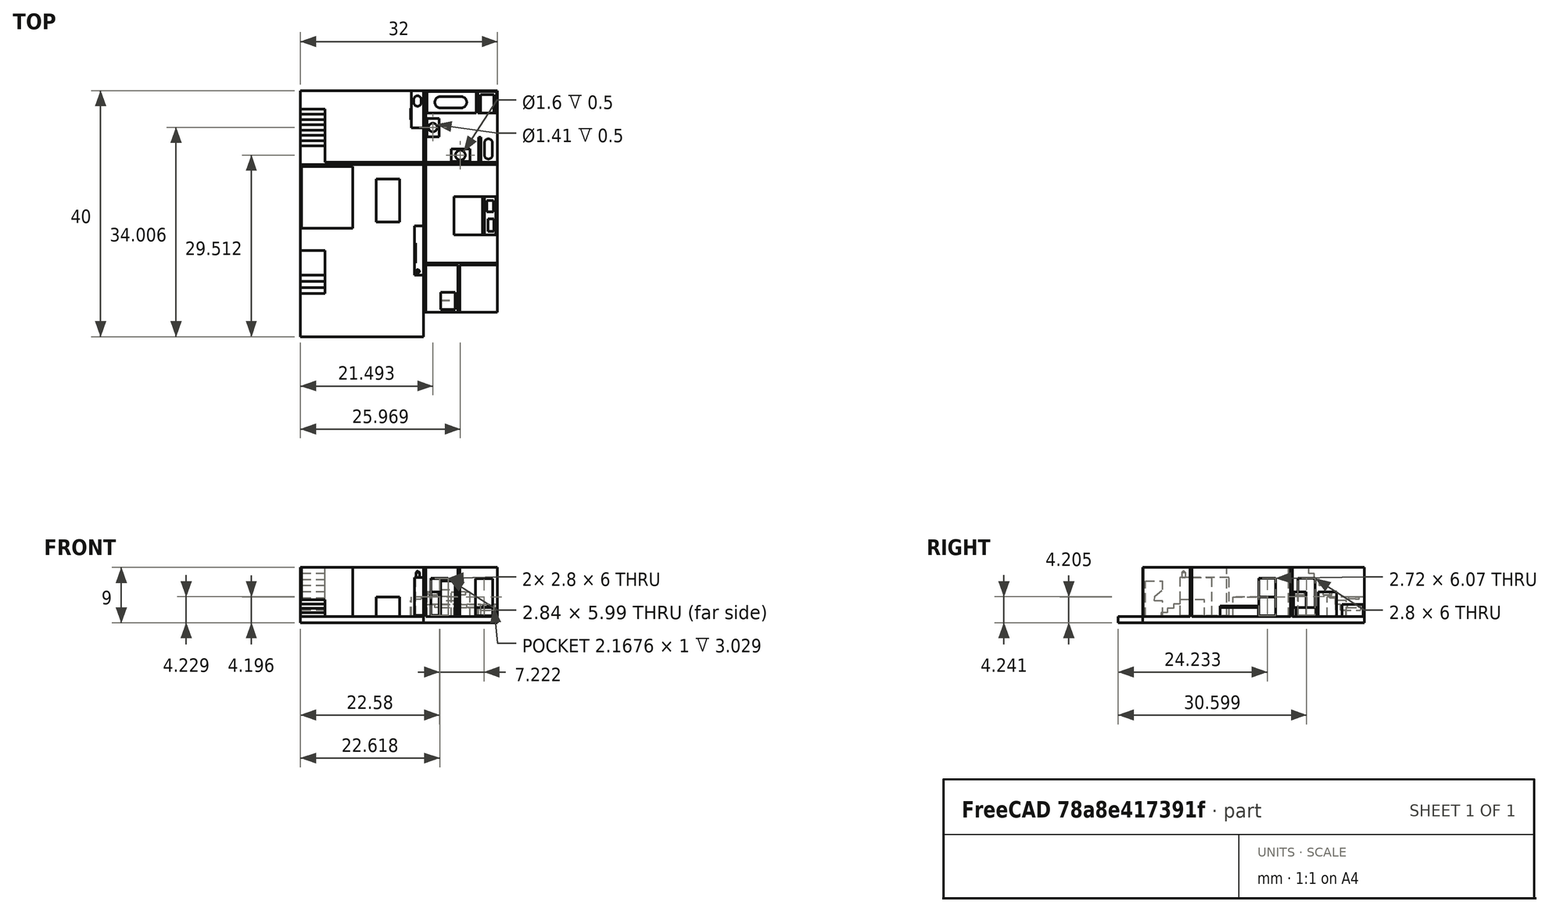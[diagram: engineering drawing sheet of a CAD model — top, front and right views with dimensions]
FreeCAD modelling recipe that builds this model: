
FCSTD DOCUMENT  (FreeCAD 0.19R)
Label: Addition1c
License: All rights reserved
LicenseURL: http://en.wikipedia.org/wiki/All_rights_reserved
objects: Sketcher::SketchObject×28, PartDesign::Pad×17, PartDesign::Pocket×10, PartDesign::Chamfer×1, PartDesign::Body×1, Mesh::Feature×1
note: 85 computed .brp shape members not serialized (recipe doc carries the construction recipe); baked Part::Feature solids carry a one-line shape summary decoded from their .brp

FEATURE [Sketcher::SketchObject] Sketch
  FullyConstrained = true
  MapMode = 5
  Support = -> [XY_Plane]
  sketch-geometry (8):
    g0: LineSegment StartX=0 StartY=-28 StartZ=0 EndX=-20 EndY=-28 EndZ=0
    g1: LineSegment StartX=-20 StartY=-28 StartZ=0 EndX=-20 EndY=0 EndZ=0
    g2: LineSegment StartX=-20 StartY=0 StartZ=0 EndX=-16 EndY=0 EndZ=0
    g3: LineSegment StartX=-16 StartY=0 StartZ=0 EndX=-16 EndY=12 EndZ=0
    g4: LineSegment StartX=-16 StartY=12 StartZ=0 EndX=12 EndY=12 EndZ=0
    g5: LineSegment StartX=12 StartY=12 StartZ=0 EndX=12 EndY=-24 EndZ=0
    g6: LineSegment StartX=12 StartY=-24 StartZ=0 EndX=0 EndY=-24 EndZ=0
    g7: LineSegment StartX=0 StartY=-24 StartZ=0 EndX=0 EndY=-28 EndZ=0
  constraints (24):
    c: Coincident(g0,g1)
    c: Horizontal(g0)
    c: Vertical(g1)
    c: DistanceX(g1) = -20
    c: DistanceY(g0) = -28
    c: Coincident(g1,g2)
    c: PointOnObject(g2,g-1)
    c: Horizontal(g2)
    c: Coincident(g2,g3)
    c: Vertical(g3)
    c: Coincident(g3,g4)
    c: Horizontal(g4)
    c: Coincident(g4,g5)
    c: Vertical(g5)
    c: Coincident(g5,g6)
    c: PointOnObject(g6,g-2)
    c: Coincident(g6,g7)
    c: Coincident(g7,g0)
    c: Vertical(g7)
    c: Horizontal(g6)
    c: Distance(g6) = 12
    c: Distance(g3) = 12
    c: DistanceY(g6) = -24
    c: DistanceX(g2) = -16
FEATURE [PartDesign::Pad] Pad  label="foundation"
  Direction = (1,1,1)
  Length = 1
  Length2 = 100
  Profile = -> Sketch
  Type = 0
FEATURE [Sketcher::SketchObject] Sketch004
  FullyConstrained = true
  MapMode = 5
  Placement = pos=(-16,0,0) rot=(0.57735,-0.57735,-0.57735;2.0944rad)
  Support = -> [Pad]
  sketch-geometry (20):
    g0: LineSegment StartX=-12 StartY=0 StartZ=0 EndX=-12 EndY=1 EndZ=0
    g1: LineSegment StartX=-12 StartY=1 StartZ=0 EndX=-9 EndY=1 EndZ=0
    g2: LineSegment StartX=-9 StartY=1 StartZ=0 EndX=-9 EndY=2 EndZ=0
    g3: LineSegment StartX=-9 StartY=2 StartZ=0 EndX=-8.14286 EndY=2 EndZ=0
    g4: LineSegment StartX=-8.14286 StartY=2 StartZ=0 EndX=-8.14286 EndY=3 EndZ=0
    g5: LineSegment StartX=-8.14286 StartY=3 StartZ=0 EndX=-7.28571 EndY=3 EndZ=0
    g6: LineSegment StartX=-7.28571 StartY=3 StartZ=0 EndX=-7.28571 EndY=4 EndZ=0
    g7: LineSegment StartX=-7.28571 StartY=4 StartZ=0 EndX=-6.42857 EndY=4 EndZ=0
    g8: LineSegment StartX=-6.42857 StartY=4 StartZ=0 EndX=-6.42857 EndY=5 EndZ=0
    g9: LineSegment StartX=-6.42857 StartY=5 StartZ=0 EndX=-5.57143 EndY=5 EndZ=0
    g10: LineSegment StartX=-5.57143 StartY=5 StartZ=0 EndX=-5.57143 EndY=6 EndZ=0
    g11: LineSegment StartX=-5.57143 StartY=6 StartZ=0 EndX=-4.71429 EndY=6 EndZ=0
    g12: LineSegment StartX=-4.71429 StartY=6 StartZ=0 EndX=-4.71429 EndY=7 EndZ=0
    g13: LineSegment StartX=-4.71429 StartY=7 StartZ=0 EndX=-3.85714 EndY=7 EndZ=0
    g14: LineSegment StartX=-3.85714 StartY=7 StartZ=0 EndX=-3.85714 EndY=8 EndZ=0
    g15: LineSegment StartX=-3.85714 StartY=8 StartZ=0 EndX=-3 EndY=8 EndZ=0
    g16: LineSegment StartX=-3 StartY=8 StartZ=0 EndX=-3 EndY=9 EndZ=0
    g17: LineSegment StartX=-3 StartY=9 StartZ=0 EndX=0 EndY=9 EndZ=0
    g18: LineSegment StartX=0 StartY=9 StartZ=0 EndX=0 EndY=0 EndZ=0
    g19: LineSegment StartX=0 StartY=0 StartZ=0 EndX=-12 EndY=0 EndZ=0
  constraints (59):
    c: PointOnObject(g0,g-1)
    c: Coincident(g0,g1)
    c: Coincident(g1,g2)
    c: Coincident(g2,g3)
    c: Coincident(g3,g4)
    c: Vertical(g4)
    c: Coincident(g4,g5)
    c: Horizontal(g5)
    c: Coincident(g5,g6)
    c: Coincident(g6,g7)
    c: Coincident(g7,g8)
    c: Coincident(g8,g9)
    c: Coincident(g9,g10)
    c: Coincident(g10,g11)
    c: Horizontal(g11)
    c: Coincident(g11,g12)
    c: Coincident(g12,g13)
    c: Coincident(g13,g14)
    c: Coincident(g14,g15)
    c: Coincident(g15,g16)
    c: Coincident(g16,g17)
    c: PointOnObject(g17,g-2)
    c: Coincident(g17,g18)
    c: Coincident(g18,g-1)
    c: Coincident(g18,g19)
    c: Coincident(g19,g0)
    c: DistanceY(g17) = 9
    c: Horizontal(g3)
    c: Horizontal(g7)
    c: Horizontal(g9)
    c: Horizontal(g13)
    c: Horizontal(g15)
    c: Vertical(g6)
    c: Vertical(g8)
    c: Vertical(g12)
    c: Vertical(g10)
    c: Vertical(g14)
    c: Vertical(g16)
    c: Vertical(g2)
    c: Equal(g2,g4)
    c: Equal(g4,g6)
    c: Equal(g6,g8)
    c: Equal(g8,g10)
    c: Equal(g10,g12)
    c: Equal(g12,g14)
    c: Equal(g14,g16)
    c: Distance(g17) = 3
    c: Equal(g3,g5)
    c: Equal(g5,g7)
    c: Equal(g7,g9)
    c: Equal(g9,g11)
    c: Equal(g11,g13)
    c: Equal(g13,g15)
    c: Horizontal(g1)
    c: Horizontal(g17)
    c: Distance(g1) = 3
    c: Vertical(g0)
    c: Distance(g0) = 1
    c: DistanceX(g0) = -12
FEATURE [Sketcher::SketchObject] Sketch007
  FullyConstrained = true
  MapMode = 5
  Placement = pos=(0,0,1) rot=(0,0,1;0rad)
  sketch-geometry (16):
    g0: LineSegment StartX=0.33 StartY=12 StartZ=0 EndX=0.33 EndY=-24 EndZ=0
    g1: LineSegment StartX=0.33 StartY=-24 StartZ=0 EndX=0 EndY=-24 EndZ=0
    g2: LineSegment StartX=0 StartY=-24 StartZ=0 EndX=0 EndY=12 EndZ=0
    g3: LineSegment StartX=0 StartY=12 StartZ=0 EndX=0.33 EndY=12 EndZ=0
    g4: LineSegment StartX=0.33 StartY=0.33 StartZ=0 EndX=12 EndY=0.33 EndZ=0
    g5: LineSegment StartX=12 StartY=0.33 StartZ=0 EndX=12 EndY=0 EndZ=0
    g6: LineSegment StartX=12 StartY=0 StartZ=0 EndX=0.33 EndY=0 EndZ=0
    g7: LineSegment StartX=0.33 StartY=0 StartZ=0 EndX=0.33 EndY=0.33 EndZ=0
    g8: LineSegment StartX=-16 StartY=0.33 StartZ=0 EndX=0 EndY=0.33 EndZ=0
    g9: LineSegment StartX=0 StartY=0.33 StartZ=0 EndX=0 EndY=0 EndZ=0
    g10: LineSegment StartX=0 StartY=0 StartZ=0 EndX=-16 EndY=0 EndZ=0
    g11: LineSegment StartX=-16 StartY=0 StartZ=0 EndX=-16 EndY=0.33 EndZ=0
    g12: LineSegment StartX=0.33 StartY=-16.33 StartZ=0 EndX=12 EndY=-16.33 EndZ=0
    g13: LineSegment StartX=12 StartY=-16.33 StartZ=0 EndX=12 EndY=-16 EndZ=0
    g14: LineSegment StartX=12 StartY=-16 StartZ=0 EndX=0.33 EndY=-16 EndZ=0
    g15: LineSegment StartX=0.33 StartY=-16 StartZ=0 EndX=0.33 EndY=-16.33 EndZ=0
  constraints (47):
    c: Coincident(g0,g1)
    c: Coincident(g1,g2)
    c: Horizontal(g1)
    c: Vertical(g0)
    c: Vertical(g2)
    c: DistanceY(g2) = 12
    c: PointOnObject(g-1,g2)
    c: Coincident(g3,g2)
    c: Coincident(g3,g0)
    c: Horizontal(g3)
    c: Distance(g3) = 0.33
    c: DistanceY(g0) = -24
    c: Coincident(g4,g5)
    c: Coincident(g5,g6)
    c: Coincident(g6,g7)
    c: Coincident(g7,g4)
    c: Horizontal(g4)
    c: Horizontal(g6)
    c: Vertical(g5)
    c: Vertical(g7)
    c: PointOnObject(g5,g-1)
    c: Coincident(g8,g9)
    c: Coincident(g9,g10)
    c: Coincident(g10,g11)
    c: Coincident(g11,g8)
    c: Horizontal(g8)
    c: Horizontal(g10)
    c: Vertical(g9)
    c: Vertical(g11)
    c: Coincident(g9,g-1)
    c: Coincident(g12,g13)
    c: Coincident(g13,g14)
    c: Coincident(g14,g15)
    c: Coincident(g15,g12)
    c: Horizontal(g12)
    c: Horizontal(g14)
    c: Vertical(g13)
    c: Vertical(g15)
    c: PointOnObject(g12,g0)
    c: Distance(g11) = 0.33
    c: Distance(g5) = 0.33
    c: DistanceX(g4) = 12
    c: DistanceX(g8) = -16
    c: PointOnObject(g4,g0)
    c: Distance(g13) = 0.33
    c: Distance(g0,g14) = 8
    c: DistanceX(g13) = 12
FEATURE [PartDesign::Pad] Pad004  label="wall"
  BaseFeature = -> Pad
  Direction = (1,1,1)
  Length = 8
  Length2 = 100
  Profile = -> Sketch007
  Type = 0
FEATURE [PartDesign::Pad] Pad005  label="stairs001"
  BaseFeature = -> Pad004
  Direction = (1,1,1)
  Length = 4
  Length2 = 100
  Profile = -> Sketch004
  Type = 0
FEATURE [Sketcher::SketchObject] Sketch008
  FullyConstrained = false
  MapMode = 5
  Placement = pos=(0,-16.33,0) rot=(1,0,0;1.5708rad)
  Support = -> [Pad005]
  sketch-geometry (8):
    g0: LineSegment StartX=1.18012 StartY=7.22945 StartZ=0 EndX=3.98012 EndY=7.22945 EndZ=0
    g1: LineSegment StartX=3.98012 StartY=7.22945 StartZ=0 EndX=3.98012 EndY=1.22945 EndZ=0
    g2: LineSegment StartX=3.98012 StartY=1.22945 StartZ=0 EndX=1.18012 EndY=1.22945 EndZ=0
    g3: LineSegment StartX=1.18012 StartY=1.22945 StartZ=0 EndX=1.18012 EndY=7.22945 EndZ=0
    g4: LineSegment StartX=8.40186 StartY=7.15703 StartZ=0 EndX=11.2019 EndY=7.15703 EndZ=0
    g5: LineSegment StartX=11.2019 StartY=7.15703 StartZ=0 EndX=11.2019 EndY=1.15703 EndZ=0
    g6: LineSegment StartX=11.2019 StartY=1.15703 StartZ=0 EndX=8.40186 EndY=1.15703 EndZ=0
    g7: LineSegment StartX=8.40186 StartY=1.15703 StartZ=0 EndX=8.40186 EndY=7.15703 EndZ=0
  constraints (20):
    c: Coincident(g0,g1)
    c: Coincident(g1,g2)
    c: Coincident(g2,g3)
    c: Coincident(g3,g0)
    c: Horizontal(g0)
    c: Horizontal(g2)
    c: Vertical(g1)
    c: Vertical(g3)
    c: Coincident(g4,g5)
    c: Coincident(g5,g6)
    c: Coincident(g6,g7)
    c: Coincident(g7,g4)
    c: Horizontal(g4)
    c: Horizontal(g6)
    c: Vertical(g5)
    c: Vertical(g7)
    c: Distance(g4) = 2.8
    c: Distance(g0) = 2.8
    c: Distance(g1) = 6
    c: Distance(g7) = 6
FEATURE [PartDesign::Pocket] Pocket
  BaseFeature = -> Pad005
  Length = 5
  Length2 = 100
  Profile = -> Sketch008
  Type = 0
FEATURE [Sketcher::SketchObject] Sketch009
  FullyConstrained = false
  MapMode = 5
  Placement = pos=(0,0,0) rot=(1,0,0;1.5708rad)
  Support = -> [Pocket]
  sketch-geometry (4):
    g0: LineSegment StartX=1.19795 StartY=7.19291 StartZ=0 EndX=4.03725 EndY=7.19291 EndZ=0
    g1: LineSegment StartX=4.03725 StartY=7.19291 StartZ=0 EndX=4.03725 EndY=1.19882 EndZ=0
    g2: LineSegment StartX=4.03725 StartY=1.19882 StartZ=0 EndX=1.19795 EndY=1.19882 EndZ=0
    g3: LineSegment StartX=1.19795 StartY=1.19882 StartZ=0 EndX=1.19795 EndY=7.19291 EndZ=0
  constraints (8):
    c: Coincident(g0,g1)
    c: Coincident(g1,g2)
    c: Coincident(g2,g3)
    c: Coincident(g3,g0)
    c: Horizontal(g0)
    c: Horizontal(g2)
    c: Vertical(g1)
    c: Vertical(g3)
FEATURE [PartDesign::Pocket] Pocket001
  BaseFeature = -> Pocket
  Length = 5
  Length2 = 100
  Profile = -> Sketch009
  Type = 0
FEATURE [Sketcher::SketchObject] Sketch010
  FullyConstrained = false
  MapMode = 5
  Placement = pos=(0.33,0,0) rot=(0.57735,0.57735,0.57735;2.0944rad)
  Support = -> [Pocket001]
  sketch-geometry (4):
    g0: LineSegment StartX=1.19868 StartY=7.24093 StartZ=0 EndX=3.99868 EndY=7.24093 EndZ=0
    g1: LineSegment StartX=3.99868 StartY=7.24093 StartZ=0 EndX=3.99868 EndY=1.24093 EndZ=0
    g2: LineSegment StartX=3.99868 StartY=1.24093 StartZ=0 EndX=1.19868 EndY=1.24093 EndZ=0
    g3: LineSegment StartX=1.19868 StartY=1.24093 StartZ=0 EndX=1.19868 EndY=7.24093 EndZ=0
  constraints (10):
    c: Coincident(g0,g1)
    c: Coincident(g1,g2)
    c: Coincident(g2,g3)
    c: Coincident(g3,g0)
    c: Horizontal(g0)
    c: Horizontal(g2)
    c: Vertical(g1)
    c: Vertical(g3)
    c: Distance(g0) = 2.8
    c: Distance(g1) = 6
FEATURE [PartDesign::Pocket] Pocket002
  BaseFeature = -> Pocket001
  Length = 5
  Length2 = 100
  Profile = -> Sketch010
  Type = 0
FEATURE [Sketcher::SketchObject] Sketch011
  FullyConstrained = false
  MapMode = 5
  Placement = pos=(0,0,1) rot=(0,0,1;0rad)
  Support = -> [Pocket002]
  sketch-geometry (8):
    g0: LineSegment StartX=0.512815 StartY=11.8677 StartZ=0 EndX=8.51282 EndY=11.8677 EndZ=0
    g1: LineSegment StartX=8.51282 StartY=11.8677 StartZ=0 EndX=8.51282 EndY=8.36765 EndZ=0
    g2: LineSegment StartX=8.51282 StartY=8.36765 StartZ=0 EndX=0.512815 EndY=8.36765 EndZ=0
    g3: LineSegment StartX=0.512815 StartY=8.36765 StartZ=0 EndX=0.512815 EndY=11.8677 EndZ=0
    g4: LineSegment StartX=8.80064 StartY=11.8358 StartZ=0 EndX=11.8627 EndY=11.8358 EndZ=0
    g5: LineSegment StartX=11.8627 StartY=11.8358 StartZ=0 EndX=11.8627 EndY=8.34693 EndZ=0
    g6: LineSegment StartX=11.8627 StartY=8.34693 StartZ=0 EndX=8.80064 EndY=8.34693 EndZ=0
    g7: LineSegment StartX=8.80064 StartY=8.34693 StartZ=0 EndX=8.80064 EndY=11.8358 EndZ=0
  constraints (18):
    c: Coincident(g0,g1)
    c: Coincident(g1,g2)
    c: Coincident(g2,g3)
    c: Coincident(g3,g0)
    c: Horizontal(g0)
    c: Horizontal(g2)
    c: Vertical(g1)
    c: Vertical(g3)
    c: Coincident(g4,g5)
    c: Coincident(g5,g6)
    c: Coincident(g6,g7)
    c: Coincident(g7,g4)
    c: Horizontal(g4)
    c: Horizontal(g6)
    c: Vertical(g5)
    c: Vertical(g7)
    c: Distance(g0) = 8
    c: Distance(g1) = 3.5
FEATURE [PartDesign::Pad] Pad006
  BaseFeature = -> Pocket002
  Direction = (1,1,1)
  Length = 2
  Length2 = 100
  Profile = -> Sketch011
  Type = 0
FEATURE [Sketcher::SketchObject] Sketch012
  FullyConstrained = false
  MapMode = 5
  Placement = pos=(0,0,1) rot=(0,0,1;0rad)
  Support = -> [Pad006]
  sketch-geometry (8):
    g0: LineSegment StartX=4.5 StartY=2.51571 StartZ=0 EndX=7.5 EndY=2.51571 EndZ=0
    g1: LineSegment StartX=7.5 StartY=2.51571 StartZ=0 EndX=7.5 EndY=0.515713 EndZ=0
    g2: LineSegment StartX=7.5 StartY=0.515713 StartZ=0 EndX=4.5 EndY=0.515713 EndZ=0
    g3: LineSegment StartX=4.5 StartY=0.515713 StartZ=0 EndX=4.5 EndY=2.51571 EndZ=0
    g4: LineSegment StartX=0.518943 StartY=7.5 StartZ=0 EndX=2.51894 EndY=7.5 EndZ=0
    g5: LineSegment StartX=2.51894 StartY=7.5 StartZ=0 EndX=2.51894 EndY=4.5 EndZ=0
    g6: LineSegment StartX=2.51894 StartY=4.5 StartZ=0 EndX=0.518943 EndY=4.5 EndZ=0
    g7: LineSegment StartX=0.518943 StartY=4.5 StartZ=0 EndX=0.518943 EndY=7.5 EndZ=0
  constraints (22):
    c: Coincident(g0,g1)
    c: Coincident(g1,g2)
    c: Coincident(g2,g3)
    c: Coincident(g3,g0)
    c: Horizontal(g0)
    c: Horizontal(g2)
    c: Vertical(g1)
    c: Vertical(g3)
    c: Distance(g3) = 2
    c: Distance(g0) = 3
    c: Coincident(g4,g5)
    c: Coincident(g5,g6)
    c: Coincident(g6,g7)
    c: Coincident(g7,g4)
    c: Horizontal(g4)
    c: Horizontal(g6)
    c: Vertical(g5)
    c: Vertical(g7)
    c: Distance(g4) = 2
    c: Distance(g5) = 3
    c: DistanceY(g6) = 4.5
    c: DistanceX(g2) = 4.5
FEATURE [PartDesign::Pad] Pad007
  BaseFeature = -> Pad006
  Direction = (1,1,1)
  Length = 4
  Length2 = 100
  Profile = -> Sketch012
  Type = 0
FEATURE [Sketcher::SketchObject] Sketch013
  FullyConstrained = false
  MapMode = 5
  Placement = pos=(0,0,1) rot=(0,0,1;0rad)
  Support = -> [Pad007]
  sketch-geometry (8):
    g0: LineSegment StartX=8.91387 StartY=4.41728 StartZ=0 EndX=9.28193 EndY=4.41728 EndZ=0
    g1: LineSegment StartX=9.28193 StartY=4.41728 StartZ=0 EndX=9.28193 EndY=0.342351 EndZ=0
    g2: LineSegment StartX=9.28193 StartY=0.342351 StartZ=0 EndX=8.91387 EndY=0.342351 EndZ=0
    g3: LineSegment StartX=8.91387 StartY=0.342351 StartZ=0 EndX=8.91387 EndY=4.41728 EndZ=0
    g4: ArcOfCircle CenterX=10.5176 CenterY=3.49717 CenterZ=0 NormalX=0 NormalY=0 NormalZ=1 AngleXU=0 Radius=0.657223 StartAngle=0 EndAngle=3.14159
    g5: ArcOfCircle CenterX=10.5176 CenterY=1.55168 CenterZ=0 NormalX=0 NormalY=0 NormalZ=1 AngleXU=0 Radius=0.657223 StartAngle=3.14159 EndAngle=6.28319
    g6: LineSegment StartX=9.86033 StartY=3.49717 StartZ=0 EndX=9.86033 EndY=1.55168 EndZ=0
    g7: LineSegment StartX=11.1748 StartY=3.49717 StartZ=0 EndX=11.1748 EndY=1.55168 EndZ=0
  constraints (14):
    c: Coincident(g0,g1)
    c: Coincident(g1,g2)
    c: Coincident(g2,g3)
    c: Coincident(g3,g0)
    c: Horizontal(g0)
    c: Horizontal(g2)
    c: Vertical(g1)
    c: Vertical(g3)
    c: Tangent(g4,g7) = 1.5708
    c: Tangent(g4,g6) = -1.5708
    c: Tangent(g6,g5) = -1.5708
    c: Tangent(g7,g5) = 1.5708
    c: Vertical(g6)
    c: Equal(g4,g5)
FEATURE [PartDesign::Pad] Pad008
  BaseFeature = -> Pad007
  Direction = (1,1,1)
  Length = 1.5
  Length2 = 100
  Profile = -> Sketch013
  Type = 0
FEATURE [Sketcher::SketchObject] Sketch014
  FullyConstrained = false
  MapMode = 5
  Placement = pos=(0,0,3) rot=(0,0,1;0rad)
  Support = -> [Pad008]
  sketch-geometry (4):
    g0: ArcOfCircle CenterX=2.72003 CenterY=10.1095 CenterZ=0 NormalX=0 NormalY=0 NormalZ=1 AngleXU=0 Radius=0.911861 StartAngle=1.5708 EndAngle=4.71239
    g1: ArcOfCircle CenterX=6.09294 CenterY=10.1095 CenterZ=0 NormalX=0 NormalY=0 NormalZ=1 AngleXU=0 Radius=0.911861 StartAngle=4.71239 EndAngle=7.85398
    g2: LineSegment StartX=2.72003 StartY=9.1976 StartZ=0 EndX=6.09294 EndY=9.1976 EndZ=0
    g3: LineSegment StartX=2.72003 StartY=11.0213 StartZ=0 EndX=6.09294 EndY=11.0213 EndZ=0
  constraints (6):
    c: Tangent(g0,g3) = 1.5708
    c: Tangent(g0,g2) = -1.5708
    c: Tangent(g2,g1) = -1.5708
    c: Tangent(g3,g1) = 1.5708
    c: Horizontal(g2)
    c: Equal(g0,g1)
FEATURE [PartDesign::Pocket] Pocket003
  BaseFeature = -> Pad008
  Length = 0.5
  Length2 = 100
  Profile = -> Sketch014
  Type = 0
FEATURE [Sketcher::SketchObject] Sketch015
  FullyConstrained = false
  MapMode = 5
  Placement = pos=(0,0,5) rot=(0,0,1;0rad)
  Support = -> [Pocket003]
  sketch-geometry (2):
    g0: Circle CenterX=1.49285 CenterY=6.00605 CenterZ=0 NormalX=0 NormalY=0 NormalZ=1 AngleXU=0 Radius=0.704239
    g1: Circle CenterX=5.96899 CenterY=1.51228 CenterZ=0 NormalX=0 NormalY=0 NormalZ=1 AngleXU=0 Radius=0.797608
FEATURE [PartDesign::Pocket] Pocket004
  BaseFeature = -> Pocket003
  Length = 0.5
  Length2 = 100
  Profile = -> Sketch015
  Type = 0
FEATURE [Sketcher::SketchObject] Sketch016
  FullyConstrained = false
  MapMode = 5
  Placement = pos=(0,0,3) rot=(0,0,1;0rad)
  Support = -> [Pocket004]
  sketch-geometry (4):
    g0: LineSegment StartX=9.25841 StartY=11.3759 StartZ=0 EndX=11.426 EndY=11.3759 EndZ=0
    g1: LineSegment StartX=11.426 StartY=11.3759 StartZ=0 EndX=11.426 EndY=7.14651 EndZ=0
    g2: LineSegment StartX=11.426 StartY=7.14651 StartZ=0 EndX=9.25841 EndY=7.14651 EndZ=0
    g3: LineSegment StartX=9.25841 StartY=7.14651 StartZ=0 EndX=9.25841 EndY=11.3759 EndZ=0
  constraints (8):
    c: Coincident(g0,g1)
    c: Coincident(g1,g2)
    c: Coincident(g2,g3)
    c: Coincident(g3,g0)
    c: Horizontal(g0)
    c: Horizontal(g2)
    c: Vertical(g1)
    c: Vertical(g3)
FEATURE [PartDesign::Pocket] Pocket005
  BaseFeature = -> Pocket004
  Length = 1
  Length2 = 100
  Profile = -> Sketch016
  Type = 0
FEATURE [Sketcher::SketchObject] Sketch017
  FullyConstrained = false
  MapMode = 5
  Placement = pos=(0.33,0,0) rot=(0.57735,0.57735,0.57735;2.0944rad)
  Support = -> [Pocket005]
  sketch-geometry (4):
    g0: LineSegment StartX=-5.12452 StartY=7.24184 StartZ=0 EndX=-2.40892 EndY=7.24184 EndZ=0
    g1: LineSegment StartX=-2.40892 StartY=7.24184 StartZ=0 EndX=-2.40892 EndY=1.16746 EndZ=0
    g2: LineSegment StartX=-2.40892 StartY=1.16746 StartZ=0 EndX=-5.12452 EndY=1.16746 EndZ=0
    g3: LineSegment StartX=-5.12452 StartY=1.16746 StartZ=0 EndX=-5.12452 EndY=7.24184 EndZ=0
  constraints (8):
    c: Coincident(g0,g1)
    c: Coincident(g1,g2)
    c: Coincident(g2,g3)
    c: Coincident(g3,g0)
    c: Horizontal(g0)
    c: Horizontal(g2)
    c: Vertical(g1)
    c: Vertical(g3)
FEATURE [PartDesign::Pocket] Pocket006
  BaseFeature = -> Pocket005
  Length = 5
  Length2 = 100
  Profile = -> Sketch017
  Type = 0
FEATURE [Sketcher::SketchObject] Sketch018
  FullyConstrained = false
  MapMode = 5
  Placement = pos=(0,0,0) rot=(0.57735,-0.57735,-0.57735;2.0944rad)
  Support = -> [Pocket006]
  sketch-geometry (4):
    g0: LineSegment StartX=10 StartY=7.38099 StartZ=0 EndX=18 EndY=7.38099 EndZ=0
    g1: LineSegment StartX=18 StartY=7.38099 StartZ=0 EndX=18 EndY=1.18099 EndZ=0
    g2: LineSegment StartX=18 StartY=1.18099 StartZ=0 EndX=10 EndY=1.18099 EndZ=0
    g3: LineSegment StartX=10 StartY=1.18099 StartZ=0 EndX=10 EndY=7.38099 EndZ=0
  constraints (11):
    c: Coincident(g0,g1)
    c: Coincident(g1,g2)
    c: Coincident(g2,g3)
    c: Coincident(g3,g0)
    c: Horizontal(g0)
    c: Horizontal(g2)
    c: Vertical(g1)
    c: Vertical(g3)
    c: Distance(g0) = 8
    c: DistanceX(g0) = 10
    c: Distance(g1) = 6.2
FEATURE [PartDesign::Pad] Pad009
  BaseFeature = -> Pocket006
  Direction = (1,1,1)
  Length = 1.5
  Length2 = 100
  Profile = -> Sketch018
  Type = 0
FEATURE [Sketcher::SketchObject] Sketch019
  FullyConstrained = false
  MapMode = 5
  Placement = pos=(0,0,1) rot=(0,0,1;0rad)
  Support = -> [Pad009]
  sketch-geometry (4):
    g0: LineSegment StartX=-19.8609 StartY=-0.34413 StartZ=0 EndX=-11.5 EndY=-0.34413 EndZ=0
    g1: LineSegment StartX=-11.5 StartY=-0.34413 StartZ=0 EndX=-11.5 EndY=-10.3441 EndZ=0
    g2: LineSegment StartX=-11.5 StartY=-10.3441 StartZ=0 EndX=-19.8609 EndY=-10.3441 EndZ=0
    g3: LineSegment StartX=-19.8609 StartY=-10.3441 StartZ=0 EndX=-19.8609 EndY=-0.34413 EndZ=0
  constraints (10):
    c: Coincident(g0,g1)
    c: Coincident(g1,g2)
    c: Coincident(g2,g3)
    c: Coincident(g3,g0)
    c: Horizontal(g0)
    c: Horizontal(g2)
    c: Vertical(g1)
    c: Vertical(g3)
    c: DistanceX(g0) = -11.5
    c: Distance(g1) = 10
FEATURE [PartDesign::Pad] Pad010
  BaseFeature = -> Pad009
  Direction = (1,1,1)
  Length = 8
  Length2 = 100
  Profile = -> Sketch019
  Type = 0
FEATURE [Sketcher::SketchObject] Sketch022
  FullyConstrained = false
  MapMode = 5
  Placement = pos=(-20,0,0) rot=(0.57735,-0.57735,-0.57735;2.0944rad)
  Support = -> [Pad010]
  sketch-geometry (10):
    g0: LineSegment StartX=21 StartY=0.958354 StartZ=0 EndX=14 EndY=0.958354 EndZ=0
    g1: LineSegment StartX=14 StartY=0.958354 StartZ=0 EndX=14 EndY=3.75835 EndZ=0
    g2: LineSegment StartX=14 StartY=3.75835 StartZ=0 EndX=18 EndY=3.75835 EndZ=0
    g3: LineSegment StartX=18 StartY=3.75835 StartZ=0 EndX=18 EndY=3.05835 EndZ=0
    g4: LineSegment StartX=18 StartY=3.05835 StartZ=0 EndX=19 EndY=3.05835 EndZ=0
    g5: LineSegment StartX=19 StartY=3.05835 StartZ=0 EndX=19 EndY=2.35835 EndZ=0
    g6: LineSegment StartX=19 StartY=2.35835 StartZ=0 EndX=20 EndY=2.35835 EndZ=0
    g7: LineSegment StartX=20 StartY=2.35835 StartZ=0 EndX=20 EndY=1.65835 EndZ=0
    g8: LineSegment StartX=20 StartY=1.65835 StartZ=0 EndX=21 EndY=1.65835 EndZ=0
    g9: LineSegment StartX=21 StartY=1.65835 StartZ=0 EndX=21 EndY=0.958354 EndZ=0
  constraints (29):
    c: Coincident(g0,g1)
    c: Horizontal(g0)
    c: Vertical(g1)
    c: Distance(g1) = 2.8
    c: DistanceX(g1) = 14
    c: Coincident(g1,g2)
    c: Horizontal(g2)
    c: Coincident(g2,g3)
    c: Coincident(g3,g4)
    c: Coincident(g4,g5)
    c: Coincident(g5,g6)
    c: Coincident(g6,g7)
    c: Coincident(g7,g8)
    c: Coincident(g8,g9)
    c: Coincident(g0,g9)
    c: Vertical(g9)
    c: Vertical(g7)
    c: Vertical(g5)
    c: Vertical(g3)
    c: Distance(g0) = 7
    c: Equal(g8,g6)
    c: Equal(g6,g4)
    c: Horizontal(g8)
    c: Horizontal(g6)
    c: Horizontal(g4)
    c: Equal(g3,g5)
    c: Equal(g5,g7)
    c: Equal(g7,g9)
    c: Distance(g2) = 4
FEATURE [PartDesign::Pad] Pad011
  BaseFeature = -> Pad010
  Direction = (1,1,1)
  Length = 4
  Length2 = 100
  Profile = -> Sketch022
  Reversed = true
  Type = 0
FEATURE [Sketcher::SketchObject] Sketch023
  FullyConstrained = false
  MapMode = 5
  Placement = pos=(0,0,1) rot=(0,0,1;0rad)
  Support = -> [Pad011]
  sketch-geometry (4):
    g0: LineSegment StartX=5.57555 StartY=-16.2289 StartZ=0 EndX=5.90555 EndY=-16.2289 EndZ=0
    g1: LineSegment StartX=5.90555 StartY=-16.2289 StartZ=0 EndX=5.90555 EndY=-23.9704 EndZ=0
    g2: LineSegment StartX=5.90555 StartY=-23.9704 StartZ=0 EndX=5.57555 EndY=-23.9704 EndZ=0
    g3: LineSegment StartX=5.57555 StartY=-23.9704 StartZ=0 EndX=5.57555 EndY=-16.2289 EndZ=0
  constraints (9):
    c: Coincident(g0,g1)
    c: Coincident(g1,g2)
    c: Coincident(g2,g3)
    c: Coincident(g3,g0)
    c: Horizontal(g0)
    c: Horizontal(g2)
    c: Vertical(g1)
    c: Vertical(g3)
    c: Distance(g2) = 0.33
FEATURE [PartDesign::Pad] Pad012  label="BRdirvider"
  BaseFeature = -> Pad011
  Direction = (1,1,1)
  Length = 8
  Length2 = 100
  Profile = -> Sketch023
  Type = 0
FEATURE [Sketcher::SketchObject] Sketch024  label="kitchenette"
  FullyConstrained = false
  MapMode = 5
  Placement = pos=(0,0,1) rot=(0,0,1;0rad)
  Support = -> [Pad012]
  sketch-geometry (4):
    g0: LineSegment StartX=-1.99946 StartY=11.9634 StartZ=0 EndX=0.000542712 EndY=11.9634 EndZ=0
    g1: LineSegment StartX=0.000542712 StartY=11.9634 StartZ=0 EndX=0.000542712 EndY=5.9634 EndZ=0
    g2: LineSegment StartX=0.000542712 StartY=5.9634 StartZ=0 EndX=-1.99946 EndY=5.9634 EndZ=0
    g3: LineSegment StartX=-1.99946 StartY=5.9634 StartZ=0 EndX=-1.99946 EndY=11.9634 EndZ=0
  constraints (10):
    c: Coincident(g0,g1)
    c: Vertical(g1)
    c: Coincident(g1,g2)
    c: Coincident(g2,g3)
    c: Coincident(g3,g0)
    c: Vertical(g3)
    c: Horizontal(g2)
    c: Distance(g2) = 2
    c: Horizontal(g0)
    c: Distance(g1) = 6
FEATURE [PartDesign::Pad] Pad013
  BaseFeature = -> Pad012
  Direction = (1,1,1)
  Length = 3.2
  Length2 = 100
  Profile = -> Sketch024
  Type = 0
FEATURE [Sketcher::SketchObject] Sketch025
  FullyConstrained = false
  MapMode = 5
  Placement = pos=(0,0,4.2) rot=(0,0,1;0rad)
  Support = -> [Pad013]
  sketch-geometry (4):
    g0: ArcOfCircle CenterX=-0.997239 CenterY=10.5422 CenterZ=0 NormalX=0 NormalY=0 NormalZ=1 AngleXU=0 Radius=0.606949 StartAngle=0 EndAngle=3.14159
    g1: ArcOfCircle CenterX=-0.997239 CenterY=10.069 CenterZ=0 NormalX=0 NormalY=0 NormalZ=1 AngleXU=0 Radius=0.606949 StartAngle=3.14159 EndAngle=6.28319
    g2: LineSegment StartX=-1.60419 StartY=10.5422 StartZ=0 EndX=-1.60419 EndY=10.069 EndZ=0
    g3: LineSegment StartX=-0.39029 StartY=10.5422 StartZ=0 EndX=-0.39029 EndY=10.069 EndZ=0
  constraints (6):
    c: Tangent(g0,g3) = 1.5708
    c: Tangent(g0,g2) = -1.5708
    c: Tangent(g2,g1) = -1.5708
    c: Tangent(g3,g1) = 1.5708
    c: Vertical(g2)
    c: Equal(g0,g1)
FEATURE [PartDesign::Pocket] Pocket007
  BaseFeature = -> Pad013
  Length = 0.35
  Length2 = 100
  Profile = -> Sketch025
  Type = 0
FEATURE [Sketcher::SketchObject] Sketch026
  FullyConstrained = false
  MapMode = 5
  Placement = pos=(-1.99946,0,0) rot=(0.57735,-0.57735,-0.57735;2.0944rad)
  Support = -> [Pocket007]
  sketch-geometry (4):
    g0: LineSegment StartX=-9.10306 StartY=3.58683 StartZ=0 EndX=-7.30306 EndY=3.58683 EndZ=0
    g1: LineSegment StartX=-7.30306 StartY=3.58683 StartZ=0 EndX=-7.30306 EndY=1.08683 EndZ=0
    g2: LineSegment StartX=-7.30306 StartY=1.08683 StartZ=0 EndX=-9.10306 EndY=1.08683 EndZ=0
    g3: LineSegment StartX=-9.10306 StartY=1.08683 StartZ=0 EndX=-9.10306 EndY=3.58683 EndZ=0
  constraints (10):
    c: Coincident(g0,g1)
    c: Coincident(g1,g2)
    c: Coincident(g2,g3)
    c: Coincident(g3,g0)
    c: Horizontal(g0)
    c: Horizontal(g2)
    c: Vertical(g1)
    c: Vertical(g3)
    c: Distance(g0) = 1.8
    c: Distance(g3) = 2.5
FEATURE [PartDesign::Pad] Pad014  label="icemaker"
  BaseFeature = -> Pocket007
  Direction = (1,1,1)
  Length = 0.1
  Length2 = 100
  Profile = -> Sketch026
  Type = 0
FEATURE [Sketcher::SketchObject] Sketch027
  FullyConstrained = false
  MapMode = 5
  Placement = pos=(-1.5,0,0) rot=(0.57735,-0.57735,-0.57735;2.0944rad)
  Support = -> [Pad014]
  sketch-geometry (4):
    g0: LineSegment StartX=12.755 StartY=7.45922 StartZ=0 EndX=16.0051 EndY=7.45922 EndZ=0
    g1: LineSegment StartX=16.0051 StartY=7.45922 StartZ=0 EndX=16.0051 EndY=1.21717 EndZ=0
    g2: LineSegment StartX=16.0051 StartY=1.21717 StartZ=0 EndX=12.755 EndY=1.21717 EndZ=0
    g3: LineSegment StartX=12.755 StartY=1.21717 StartZ=0 EndX=12.755 EndY=7.45922 EndZ=0
  constraints (8):
    c: Coincident(g0,g1)
    c: Coincident(g1,g2)
    c: Coincident(g2,g3)
    c: Coincident(g3,g0)
    c: Horizontal(g0)
    c: Horizontal(g2)
    c: Vertical(g1)
    c: Vertical(g3)
FEATURE [PartDesign::Pocket] Pocket008
  BaseFeature = -> Pad014
  Length = 0.2
  Length2 = 100
  Profile = -> Sketch027
  Type = 0
FEATURE [Sketcher::SketchObject] Sketch028
  FullyConstrained = false
  MapMode = 5
  Placement = pos=(0,0,7.38099) rot=(0,0,1;0rad)
  Support = -> [Pocket008]
  sketch-geometry (1):
    g0: Circle CenterX=-0.970954 CenterY=-17.3767 CenterZ=0 NormalX=0 NormalY=0 NormalZ=1 AngleXU=0 Radius=0.280145
FEATURE [PartDesign::Pad] Pad015
  BaseFeature = -> Pocket008
  Direction = (1,1,1)
  Length = 1
  Length2 = 100
  Profile = -> Sketch028
  Type = 0
FEATURE [PartDesign::Chamfer] Chamfer
  Angle = 45
  Base = -> Pad015 [Edge377]
  BaseFeature = -> Pad015
  ChamferType = 0
  FlipDirection = false
  Size = 0.2
  Size2 = 1
  SupportTransform = false
FEATURE [Sketcher::SketchObject] Sketch033
  FullyConstrained = false
  MapMode = 5
  Placement = pos=(0,0,1) rot=(0,0,1;0rad)
  Support = -> [Chamfer]
  sketch-geometry (4):
    g0: LineSegment StartX=2.74629 StartY=-20.7806 StartZ=0 EndX=5.14629 EndY=-20.7806 EndZ=0
    g1: LineSegment StartX=5.14629 StartY=-20.7806 StartZ=0 EndX=5.14629 EndY=-23.5806 EndZ=0
    g2: LineSegment StartX=5.14629 StartY=-23.5806 StartZ=0 EndX=2.74629 EndY=-23.5806 EndZ=0
    g3: LineSegment StartX=2.74629 StartY=-23.5806 StartZ=0 EndX=2.74629 EndY=-20.7806 EndZ=0
  constraints (10):
    c: Coincident(g0,g1)
    c: Coincident(g1,g2)
    c: Coincident(g2,g3)
    c: Coincident(g3,g0)
    c: Horizontal(g0)
    c: Horizontal(g2)
    c: Vertical(g1)
    c: Vertical(g3)
    c: Distance(g0) = 2.4
    c: Distance(g3) = 2.8
FEATURE [PartDesign::Pad] Pad016
  BaseFeature = -> Chamfer
  Direction = (1,1,1)
  Length = 5.8
  Length2 = 100
  Profile = -> Sketch033
  Type = 0
FEATURE [Sketcher::SketchObject] Sketch034
  FullyConstrained = false
  MapMode = 5
  Placement = pos=(2.74629,0,0) rot=(0.57735,-0.57735,-0.57735;2.0944rad)
  Support = -> [Pad016]
  sketch-geometry (4):
    g0: LineSegment StartX=20.6066 StartY=3.56678 StartZ=0 EndX=22.097 EndY=3.56678 EndZ=0
    g1: LineSegment StartX=22.097 StartY=3.56678 StartZ=0 EndX=22.0697 EndY=4.30513 EndZ=0
    g2: LineSegment StartX=22.0697 StartY=4.30513 StartZ=0 EndX=20.6066 EndY=5.53571 EndZ=0
    g3: LineSegment StartX=20.6066 StartY=5.53571 StartZ=0 EndX=20.6066 EndY=3.56678 EndZ=0
  constraints (6):
    c: Horizontal(g0)
    c: Coincident(g0,g1)
    c: Coincident(g1,g2)
    c: Coincident(g2,g3)
    c: Coincident(g3,g0)
    c: Vertical(g3)
FEATURE [PartDesign::Pocket] Pocket009
  BaseFeature = -> Pad016
  Length = 2.5
  Length2 = 100
  Profile = -> Sketch034
  Type = 0
FEATURE [Sketcher::SketchObject] Sketch035
  FullyConstrained = true
  MapMode = 5
  Placement = pos=(0,0,0) rot=(1,0,0;3.14159rad)
  Support = -> [Pocket009]
FEATURE [Sketcher::SketchObject] Sketch036
  FullyConstrained = false
  MapMode = 5
  Placement = pos=(0,0,1) rot=(0,0,1;0rad)
  Support = -> [Pocket009]
  sketch-geometry (4):
    g0: LineSegment StartX=-7.7165 StartY=-2.34711 StartZ=0 EndX=-3.9165 EndY=-2.34711 EndZ=0
    g1: LineSegment StartX=-3.9165 StartY=-2.34711 StartZ=0 EndX=-3.9165 EndY=-9.34711 EndZ=0
    g2: LineSegment StartX=-3.9165 StartY=-9.34711 StartZ=0 EndX=-7.7165 EndY=-9.34711 EndZ=0
    g3: LineSegment StartX=-7.7165 StartY=-9.34711 StartZ=0 EndX=-7.7165 EndY=-2.34711 EndZ=0
  constraints (10):
    c: Coincident(g0,g1)
    c: Coincident(g1,g2)
    c: Coincident(g2,g3)
    c: Coincident(g3,g0)
    c: Horizontal(g0)
    c: Horizontal(g2)
    c: Vertical(g1)
    c: Vertical(g3)
    c: Distance(g0) = 3.8
    c: Distance(g3) = 7
FEATURE [PartDesign::Pad] Pad017
  BaseFeature = -> Pocket009
  Direction = (1,1,1)
  Length = 3.2
  Length2 = 100
  Profile = -> Sketch036
  Type = 0
FEATURE [Sketcher::SketchObject] Sketch037
  FullyConstrained = false
  MapMode = 5
  Placement = pos=(0,0,1) rot=(0,0,1;0rad)
  Support = -> [Pad017]
  sketch-geometry (4):
    g0: LineSegment StartX=4.92681 StartY=-5.23214 StartZ=0 EndX=11.7268 EndY=-5.23214 EndZ=0
    g1: LineSegment StartX=11.7268 StartY=-5.23214 StartZ=0 EndX=11.7268 EndY=-11.4321 EndZ=0
    g2: LineSegment StartX=11.7268 StartY=-11.4321 StartZ=0 EndX=4.92681 EndY=-11.4321 EndZ=0
    g3: LineSegment StartX=4.92681 StartY=-11.4321 StartZ=0 EndX=4.92681 EndY=-5.23214 EndZ=0
  constraints (10):
    c: Coincident(g0,g1)
    c: Coincident(g1,g2)
    c: Coincident(g2,g3)
    c: Coincident(g3,g0)
    c: Horizontal(g0)
    c: Horizontal(g2)
    c: Vertical(g1)
    c: Vertical(g3)
    c: Distance(g1) = 6.2
    c: Distance(g0) = 6.8
FEATURE [PartDesign::Pad] Pad018
  BaseFeature = -> Pad017
  Direction = (1,1,1)
  Length = 1.5
  Length2 = 100
  Profile = -> Sketch037
  Type = 0
FEATURE [Sketcher::SketchObject] Sketch038
  FullyConstrained = false
  MapMode = 5
  Placement = pos=(0,0,2.5) rot=(0,0,1;0rad)
  Support = -> [Pad018]
  sketch-geometry (12):
    g0: LineSegment StartX=9.53341 StartY=-5.24295 StartZ=0 EndX=9.88639 EndY=-5.24295 EndZ=0
    g1: LineSegment StartX=9.88639 StartY=-5.24295 StartZ=0 EndX=9.88639 EndY=-11.4476 EndZ=0
    g2: LineSegment StartX=9.88639 StartY=-11.4476 StartZ=0 EndX=9.53341 EndY=-11.4476 EndZ=0
    g3: LineSegment StartX=9.53341 StartY=-11.4476 StartZ=0 EndX=9.53341 EndY=-5.24295 EndZ=0
    g4: LineSegment StartX=10.2899 StartY=-5.85344 StartZ=0 EndX=11.3415 EndY=-5.85344 EndZ=0
    g5: LineSegment StartX=11.3415 StartY=-5.85344 StartZ=0 EndX=11.3415 EndY=-7.69373 EndZ=0
    g6: LineSegment StartX=11.3415 StartY=-7.69373 StartZ=0 EndX=10.2899 EndY=-7.69373 EndZ=0
    g7: LineSegment StartX=10.2899 StartY=-7.69373 StartZ=0 EndX=10.2899 EndY=-5.85344 EndZ=0
    g8: LineSegment StartX=10.4477 StartY=-8.87677 StartZ=0 EndX=11.3941 EndY=-8.87677 EndZ=0
    g9: LineSegment StartX=11.3941 StartY=-8.87677 StartZ=0 EndX=11.3941 EndY=-10.8485 EndZ=0
    g10: LineSegment StartX=11.3941 StartY=-10.8485 StartZ=0 EndX=10.4477 EndY=-10.8485 EndZ=0
    g11: LineSegment StartX=10.4477 StartY=-10.8485 StartZ=0 EndX=10.4477 EndY=-8.87677 EndZ=0
  constraints (24):
    c: Coincident(g0,g1)
    c: Coincident(g1,g2)
    c: Coincident(g2,g3)
    c: Coincident(g3,g0)
    c: Horizontal(g0)
    c: Horizontal(g2)
    c: Vertical(g1)
    c: Vertical(g3)
    c: Coincident(g4,g5)
    c: Coincident(g5,g6)
    c: Coincident(g6,g7)
    c: Coincident(g7,g4)
    c: Horizontal(g4)
    c: Horizontal(g6)
    c: Vertical(g5)
    c: Vertical(g7)
    c: Coincident(g8,g9)
    c: Coincident(g9,g10)
    c: Coincident(g10,g11)
    c: Coincident(g11,g8)
    c: Horizontal(g8)
    c: Horizontal(g10)
    c: Vertical(g9)
    c: Vertical(g11)
FEATURE [PartDesign::Pad] Pad019
  BaseFeature = -> Pad018
  Direction = (1,1,1)
  Length = 0.2
  Length2 = 100
  Profile = -> Sketch038
  Type = 0
FEATURE [PartDesign::Body] Body
  Group = -> [Sketch,Pad,Sketch004,Sketch007,Pad004,Pad005,Sketch008,Pocket,Sketch009,Pocket001,Sketch010,Pocket002,Sketch011,Pad006,Sketch012,Pad007,Sketch013,Pad008,Sketch014,Pocket003,Sketch015,Pocket004,Sketch016,Pocket005,Sketch017,Pocket006,Sketch018,Pad009,Sketch019,Pad010,Sketch022,Pad011,Sketch023,Pad012,Sketch024,Pad013,Sketch025,Pocket007,Sketch026,Pad014,Sketch027,Pocket008,Sketch028,Pad015,Chamfer,+11 more]
  Origin = -> Origin
  Tip = -> Pad019
FEATURE [Mesh::Feature] Mesh  label="Pad019 (Meshed)"
